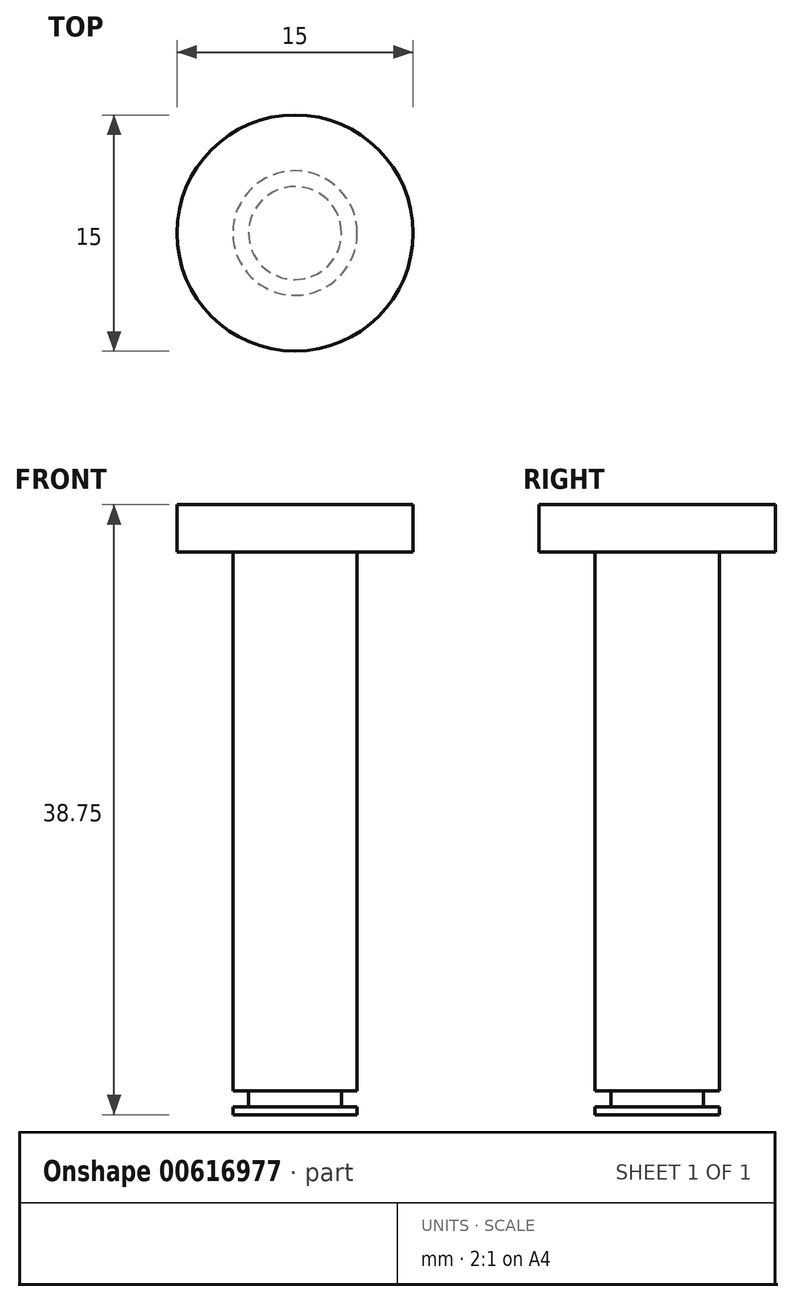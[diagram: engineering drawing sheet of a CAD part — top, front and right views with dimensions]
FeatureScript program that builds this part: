
annotation { "Feature Type Name" : "Feature", "Feature Type Description" : "" }
export const myFeature = defineFeature(function(context is Context, id is Id, definition is map)
    precondition{}
    {
        {
            var Q0;
            Q0=qCreatedBy(makeId("Front.planeOp"),FACE);
            var sketch = newSketch(context, id + "F0", { "sketchPlane" : qUnion([Q0])});
            skLineSegment(sketch, "E0", {"start": v(0, 0) * mm, "end": v(3.95, 0) * mm});
            skLineSegment(sketch, "E1", {"start": v(3.95, 0) * mm, "end": v(3.95, 35.75) * mm});
            skLineSegment(sketch, "E2", {"start": v(7.5, 38.75) * mm, "end": v(0, 38.75) * mm});
            skLineSegment(sketch, "E3", {"start": v(0, 38.75) * mm, "end": v(0, 0) * mm});
            skLineSegment(sketch, "E4.bottom", {"start": v(3.95, 1.5) * mm, "end": v(2.95, 1.5) * mm});
            skLineSegment(sketch, "E4.top", {"start": v(3.95, 0.5) * mm, "end": v(2.95, 0.5) * mm});
            skLineSegment(sketch, "E4.left", {"start": v(3.95, 1.5) * mm, "end": v(3.95, 0.5) * mm});
            skLineSegment(sketch, "E4.right", {"start": v(2.95, 1.5) * mm, "end": v(2.95, 0.5) * mm});
            skLineSegment(sketch, "E5", {"start": v(3.95, 35.75) * mm, "end": v(7.5, 35.75) * mm});
            skLineSegment(sketch, "E6", {"start": v(7.5, 35.75) * mm, "end": v(7.5, 38.75) * mm});
            skSolve(sketch);
        }
        {
            var Q0;
            {var subQ4=sQuery(id+"F0.wireOp",EDGE,"E0");Q0=makeQuery(id+"F0.imprint","IMPRINT",FACE,{"disambiguationData":[TD([[makeQuery(id+"F0.imprint","IMPRINT",EDGE,{"derivedFrom":subQ4}),1.0]])]});}
            var Q1;
            Q1=sQuery(id+"F0.wireOp",EDGE,"E3");
            revolve(context, id + "F1", {"entities" : qUnion([Q0]), "axis" : qUnion([Q1]), "revolveType" : RevolveType.FULL});
        }
    });
